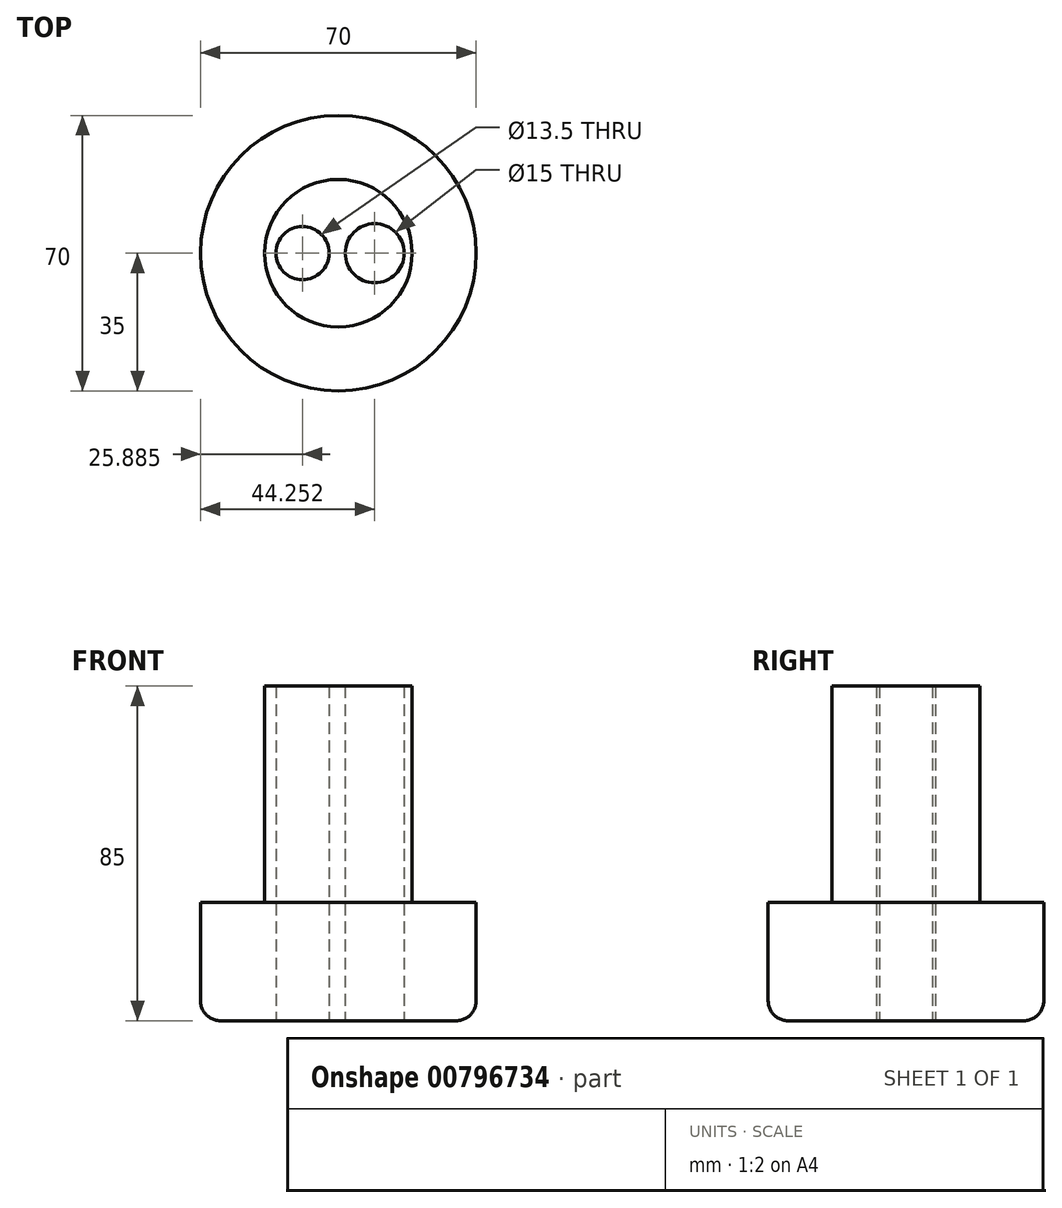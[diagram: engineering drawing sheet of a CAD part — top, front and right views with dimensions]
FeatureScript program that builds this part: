
annotation { "Feature Type Name" : "Feature", "Feature Type Description" : "" }
export const myFeature = defineFeature(function(context is Context, id is Id, definition is map)
    precondition{}
    {
        {
            var Q0;
            Q0=qCreatedBy(makeId("Top.planeOp"),FACE);
            var sketch = newSketch(context, id + "F0", { "sketchPlane" : qUnion([Q0])});
            skCircle(sketch, "E0", {"center": v(0, 0) * mm, "radius": 18.75 * mm});
            skCircle(sketch, "E1", {"center": v(-9.12, 0) * mm, "radius": 6.75 * mm});
            skCircle(sketch, "E2", {"center": v(9.25, 0) * mm, "radius": 7.5 * mm});
            skCircle(sketch, "E3", {"center": v(0, 0) * mm, "radius": 35 * mm});
            skSolve(sketch);
        }
        {
            var Q0;
            Q0=makeQuery(id+"F0.imprint","IMPRINT",FACE,{"disambiguationData":[TD([[makeQuery(id+"F0.imprint","IMPRINT",EDGE,{"derivedFrom":sQuery(id+"F0.wireOp",EDGE,"E0")}),-1.0]])]});
            extrude(context, id + "F1", {"entities" : qUnion([Q0]), "depth" : 30 * mm, "offsetDistance" : 25 * mm});
        }
        {
            var Q0;
            Q0=makeQuery(id+"F0.imprint","IMPRINT",FACE,{"disambiguationData":[TD([[makeQuery(id+"F0.imprint","IMPRINT",EDGE,{"derivedFrom":sQuery(id+"F0.wireOp",EDGE,"E0")}),1.0]])]});
            extrude(context, id + "F2", {"entities" : qUnion([Q0]), "operationType" : NewBodyOperationType.ADD, "depth" : 85 * mm, "offsetDistance" : 25 * mm});
        }
        {
            var Q0;
            Q0=makeQuery(id+"F1.opExtrude","CAP_EDGE",EDGE,{"disambiguationData":[OSD([sQuery(id+"F0.wireOp",EDGE,"E3")])],"isStart":true});
            fillet(context, id + "F3", {"entities" : qUnion([Q0]), "radius" : 5 * mm, "tangentPropagation" : true, "allowEdgeOverflow" : false});
        }
    });
